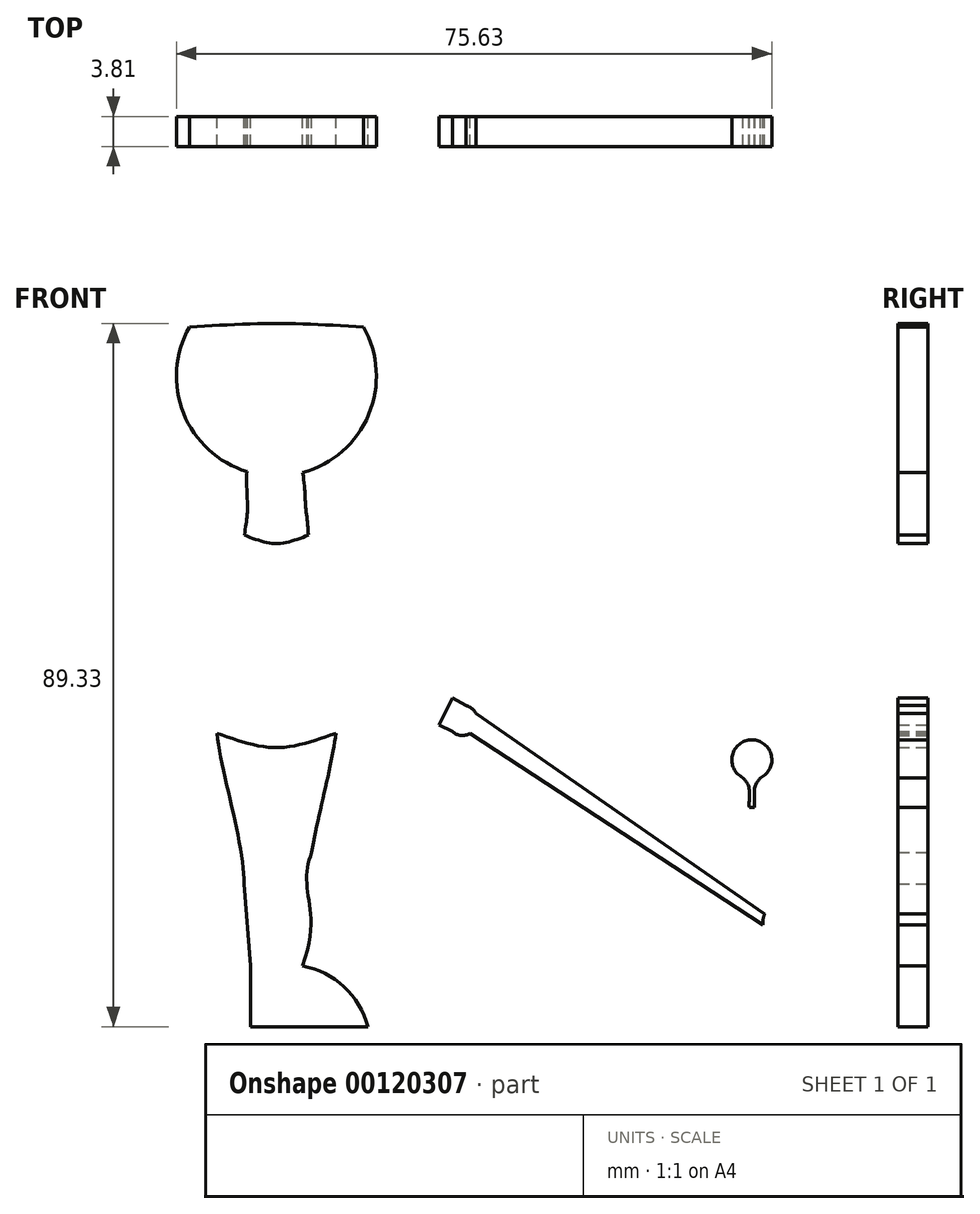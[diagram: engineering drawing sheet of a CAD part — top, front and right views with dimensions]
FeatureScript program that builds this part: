
annotation { "Feature Type Name" : "Feature", "Feature Type Description" : "" }
export const myFeature = defineFeature(function(context is Context, id is Id, definition is map)
    precondition{}
    {
        {
            var Q0;
            Q0=qCreatedBy(makeId("Front.planeOp"),FACE);
            var sketch = newSketch(context, id + "F0", { "sketchPlane" : qUnion([Q0])});
            skArc(sketch, "E0", {"start": v(3.35, -12.25) * mm, "mid": v(11.72, -4.89) * mm, "end": v(11.06, 6.24) * mm});
            skPoint(sketch, "E1.start.orphan", {"position": v(0, -12.7) * mm});
            skFitSpline(sketch, "E2", {"points": [v(-3.74, -12.14) * mm, v(-3.67, -16.75) * mm, v(-4.06, -20.2) * mm], "startDerivative": vector(-0.81, -8.16) * mm, "endDerivative": vector(-1.27, -8.97) * mm});
            skFitSpline(sketch, "E3", {"points": [v(3.35, -12.25) * mm, v(3.73, -16.69) * mm, v(4.06, -20.2) * mm], "startDerivative": vector(1.66, -10.86) * mm, "endDerivative": vector(0.18, -7.59) * mm});
            skPoint(sketch, "E4.middle", {"position": v(0, -38.64) * mm});
            skFitSpline(sketch, "E5", {"points": [v(-4.06, -20.2) * mm, v(-7.56, -24.62) * mm, v(-7.56, -30.14) * mm, v(-7.27, -38.17) * mm, v(-7.56, -45.36) * mm, v(-4.14, -64.52) * mm], "startDerivative": vector(-27.34, -19.73) * mm, "endDerivative": vector(-1.25, -47.28) * mm});
            skPoint(sketch, "E6.orphan", {"position": v(-7.56, -20.61) * mm});
            skLineSegment(sketch, "E7.trimOffspring", {"start": v(-7.56, -45.36) * mm, "end": v(-7.56, -45.36) * mm});
            skFitSpline(sketch, "E8.MirrorCS", {"points": [v(4.06, -20.2) * mm, v(7.56, -24.62) * mm, v(7.56, -30.14) * mm, v(7.27, -38.17) * mm, v(7.56, -45.36) * mm, v(4.14, -64.52) * mm], "startDerivative": vector(27.34, -19.73) * mm, "endDerivative": vector(1.25, -47.28) * mm});
            skPoint(sketch, "E9.orphan", {"position": v(7.56, -20.61) * mm});
            skLineSegment(sketch, "E10.trimOffspring", {"start": v(7.56, -45.36) * mm, "end": v(7.56, -45.36) * mm});
            skPoint(sketch, "E11.orphan", {"position": v(-7.56, -56.66) * mm});
            skPoint(sketch, "E12.orphan", {"position": v(7.56, -56.66) * mm});
            skPoint(sketch, "E13.center.orphan", {"position": v(0, 12.7) * mm});
            skLineSegment(sketch, "E14", {"start": v(11.06, 6.24) * mm, "end": v(21.67, 6.24) * mm});
            skLineSegment(sketch, "E15", {"start": v(21.67, 6.24) * mm, "end": v(21.67, 8.54) * mm});
            skLineSegment(sketch, "E16", {"start": v(21.67, 8.54) * mm, "end": v(9.4, 8.54) * mm});
            skLineSegment(sketch, "E17", {"start": v(-4.14, -64.52) * mm, "end": v(-3.3, -74.93) * mm});
            skPoint(sketch, "E18.orphan", {"position": v(4.14, -78.64) * mm});
            skLineSegment(sketch, "E19", {"start": v(-3.3, -74.93) * mm, "end": v(-3.3, -82.64) * mm});
            skLineSegment(sketch, "E20", {"start": v(-3.3, -82.64) * mm, "end": v(11.6, -82.64) * mm});
            skArc(sketch, "E21", {"start": v(11.6, -82.64) * mm, "mid": v(8.57, -77.59) * mm, "end": v(3.3, -74.93) * mm});
            skArc(sketch, "E22.trimOffspring", {"start": v(9.4, 8.54) * mm, "mid": v(-10.72, 6.81) * mm, "end": v(-3.74, -12.14) * mm});
            skPoint(sketch, "E23.1.internal.orphan", {"position": v(21.5, -30.14) * mm});
            skFitSpline(sketch, "E24", {"points": [v(7.56, -45.36) * mm, v(6.18, -56.66) * mm, v(4.14, -61.5) * mm, v(4.01, -65.83) * mm, v(3.3, -74.93) * mm], "startDerivative": vector(-2.74, -39.56) * mm, "endDerivative": vector(-17.53, -48.3) * mm});
            skLineSegment(sketch, "E25", {"start": v(7.23, -37.57) * mm, "end": v(22.8, -45.39) * mm});
            skLineSegment(sketch, "E26", {"start": v(24.46, -42.07) * mm, "end": v(7.32, -32.73) * mm});
            skLineSegment(sketch, "E27", {"start": v(7.87, -27.1) * mm, "end": v(7.42, -31.56) * mm});
            skArc(sketch, "E28", {"start": v(22.35, -45.16) * mm, "mid": v(23.44, -45.64) * mm, "end": v(24.6, -45.39) * mm});
            skPoint(sketch, "E29.start.orphan", {"position": v(25.34, -44.62) * mm});
            skLineSegment(sketch, "E30", {"start": v(24.6, -45.39) * mm, "end": v(61.8, -69.72) * mm});
            skLineSegment(sketch, "E31", {"start": v(62.01, -68.3) * mm, "end": v(25.34, -42.84) * mm});
            skArc(sketch, "E32", {"start": v(67.88, -68.81) * mm, "mid": v(67.88, -68.7) * mm, "end": v(67.88, -68.58) * mm});
            skPoint(sketch, "E33.1.internal.snap0", {"position": v(63.92, -66.68) * mm});
            skPoint(sketch, "E33.4.internal.snap0", {"position": v(66.56, -72.97) * mm});
            skPoint(sketch, "E33.5.internal.snap0", {"position": v(63.92, -66.68) * mm});
            skFitSpline(sketch, "E33", {"points": [v(61.8, -69.72) * mm, v(63.92, -71.95) * mm, v(66.56, -72.97) * mm, v(67.88, -68.58) * mm, v(66.56, -64.33) * mm, v(63.92, -65.46) * mm, v(61.8, -69.72) * mm]});
            skPoint(sketch, "E34.start.orphan", {"position": v(66.03, -63.63) * mm});
            skPoint(sketch, "E35.end.orphan", {"position": v(62.5, -68.65) * mm});
            skArc(sketch, "E36", {"start": v(61.49, -51.04) * mm, "mid": v(60.4, -46.2) * mm, "end": v(59.3, -51.04) * mm});
            skCircle(sketch, "E37", {"center": v(39.32, -39.03) * mm, "radius": 1.27 * mm});
            skLineSegment(sketch, "E38", {"start": v(60.4, -54.78) * mm, "end": v(60.4, -59.72) * mm});
            skFitSpline(sketch, "E39", {"points": [v(59.3, -51.04) * mm, v(60, -52.23) * mm, v(60.04, -54.34) * mm, v(60.08, -54.78) * mm], "startDerivative": vector(2.49, -2.76) * mm, "endDerivative": vector(0.3, -1.65) * mm});
            skFitSpline(sketch, "E40.MirrorCS", {"points": [v(61.49, -51.04) * mm, v(60.77, -52.23) * mm, v(60.74, -54.34) * mm, v(60.7, -54.78) * mm], "startDerivative": vector(-2.49, -2.76) * mm, "endDerivative": vector(-0.3, -1.65) * mm});
            skLineSegment(sketch, "E41", {"start": v(60.08, -54.78) * mm, "end": v(60.7, -54.78) * mm});
            skLineSegment(sketch, "E42", {"start": v(7.27, -37.6) * mm, "end": v(7.27, -38.17) * mm});
            skPoint(sketch, "E43.1.internal.orphan", {"position": v(0, 6.7) * mm});
            skArc(sketch, "E44.trimOffspring", {"start": v(25.34, -42.84) * mm, "mid": v(24.81, -42.2) * mm, "end": v(24.08, -41.86) * mm});
            skFitSpline(sketch, "E45", {"points": [v(11.06, 6.24) * mm, v(0, 6.7) * mm, v(-11.06, 6.24) * mm], "startDerivative": vector(-22.12, 1.35) * mm, "endDerivative": vector(-22.12, -1.35) * mm});
            skFitSpline(sketch, "E46", {"points": [v(4.06, -20.2) * mm, v(0, -21.26) * mm, v(-4.06, -20.2) * mm], "startDerivative": vector(-8.12, -3.2) * mm, "endDerivative": vector(-8.12, 3.2) * mm});
            skFitSpline(sketch, "E47", {"points": [v(7.56, -45.36) * mm, v(0, -47.18) * mm, v(-7.56, -45.36) * mm], "startDerivative": vector(-15.12, -5.46) * mm, "endDerivative": vector(-15.12, 5.46) * mm});
            skFitSpline(sketch, "E48", {"points": [v(3.3, -74.93) * mm, v(-3.24, -74.93) * mm], "startDerivative": vector(-5.17, 0) * mm, "endDerivative": vector(-9.71, 2.73) * mm});
            skPoint(sketch, "E49.end.orphan", {"position": v(0, -79.33) * mm});
            skLineSegment(sketch, "E50", {"start": v(22.35, -40.91) * mm, "end": v(20.64, -44.3) * mm});
            skSolve(sketch);
        }
        {
            var Q0;
            Q0=makeQuery(id+"F0.imprint","IMPRINT",FACE,{"disambiguationData":[TD([[makeQuery(id+"F0.imprint","IMPRINT",EDGE,{"derivedFrom":sQuery(id+"F0.wireOp",EDGE,"E0")}),1.0]])]});
            var Q1;
            {var subQ1=sQuery(id+"F0.wireOp",EDGE,"E17");Q1=makeQuery(id+"F0.imprint","IMPRINT",FACE,{"disambiguationData":[TD([[makeQuery(id+"F0.imprint","IMPRINT",EDGE,{"derivedFrom":subQ1}),1.0]])]});}
            extrude(context, id + "F1", {"entities" : qUnion([Q0, Q1]), "depth" : 3.8 * mm});
        }
        {
            var Q0;
            {var subQ4=sQuery(id+"F0.wireOp",EDGE,"E25");var subQ8=sQuery(id+"F0.wireOp",EDGE,"E5");var subQ9=makeQuery(id+"F0.imprint","INTERSECT",VERTEX,{"derivedFrom":[subQ8,subQ4]});Q0=makeQuery(id+"F0.imprint","IMPRINT",FACE,{"disambiguationData":[TD([[makeQuery(id+"F0.imprint","IMPRINT",EDGE,{"disambiguationData":[TD([[subQ9,1.0]])],"derivedFrom":subQ8}),1.0]])]});}
            extrude(context, id + "F2", {"entities" : qUnion([Q0]), "depth" : 3.8 * mm});
        }
        {
            var Q0;
            {var subQ1=sQuery(id+"F0.wireOp",EDGE,"E30");Q0=makeQuery(id+"F0.imprint","IMPRINT",FACE,{"disambiguationData":[TD([[makeQuery(id+"F0.imprint","IMPRINT",EDGE,{"derivedFrom":subQ1}),1.0]])]});}
            var Q1;
            Q1=makeQuery(id+"F0.imprint","IMPRINT",FACE,{"disambiguationData":[TD([[makeQuery(id+"F0.imprint","IMPRINT",EDGE,{"derivedFrom":sQuery(id+"F0.wireOp",EDGE,"E36")}),1.0]])]});
            extrude(context, id + "F3", {"entities" : qUnion([Q0, Q1]), "operationType" : NewBodyOperationType.ADD, "depth" : 3.8 * mm});
        }
    });
